# Revit family: CMP 350 V.V. EasyPlug
name_source: partatom
category: Equipement spécialisé
units: mm (PartAtom-declared; Revit-internal decimal feet)

## family parameters
Basée sur le plan de construction = Non
Conserver l'orientation des annotations = Non
Cote de connecteur circulaire = Utiliser le rayon
Couper avec des vides une fois chargée = Non
Numéro OmniClass = 23.40.40.14.14.11
Partagée = Non
Repère de localisation dans la pièce = Non
Titre OmniClass = Food Mixers
Toujours verticalement = Oui
Type d'élément = Normal

## types (5) — shared parameters
Apparent Power = 0 VA
Depth = 95 mm
Depth Electrique connexion = 48 mm
Description = MIXERS PLONGEANTS GAMME COMPACTE CMP
Fabricant = ROBOT COUPE
Height = 727 mm
Height Electrique connexion = 716 mm
Modèle = CMP 350 V.V. EasyPlug
Phase = 1
Speeds (Rpm) = 2300 to 9600
URL = www.robot-coupe.com
Watts = 400 W
Weight = 3.5 kg
Width = 201 mm
water = Connector
zero-valued in all types: Cold water supply, Cold water supply height, Elévation par défaut, Used water, Waste water height

## per-type parameters (varying)
| type | Amps | Cycle | Volts |
| CMP 350 V.V.   EasyPlug   230/50/1 | 1.7 A | 50 Hz | 230 V |
| CMP 350 V.V.   EasyPlug   240/50/1 UK plug | 1.7 A | 50 Hz | 240 V |
| CMP 350 V.V.   EasyPlug   120/60/1 | 3.1 A | 60 Hz | 120 V |
| CMP 350 V.V.   EasyPlug   220/60/1 | 1.6 A | 60 Hz | 220 V |
| CMP 350 V.V.   EasyPlug   220/60/1 SAU | 1.6 A | 60 Hz | 220 V |

## geometry (parser evidence)
native form markers: Blend x86, Sweep x4
no freeform markers — native parametric forms only
